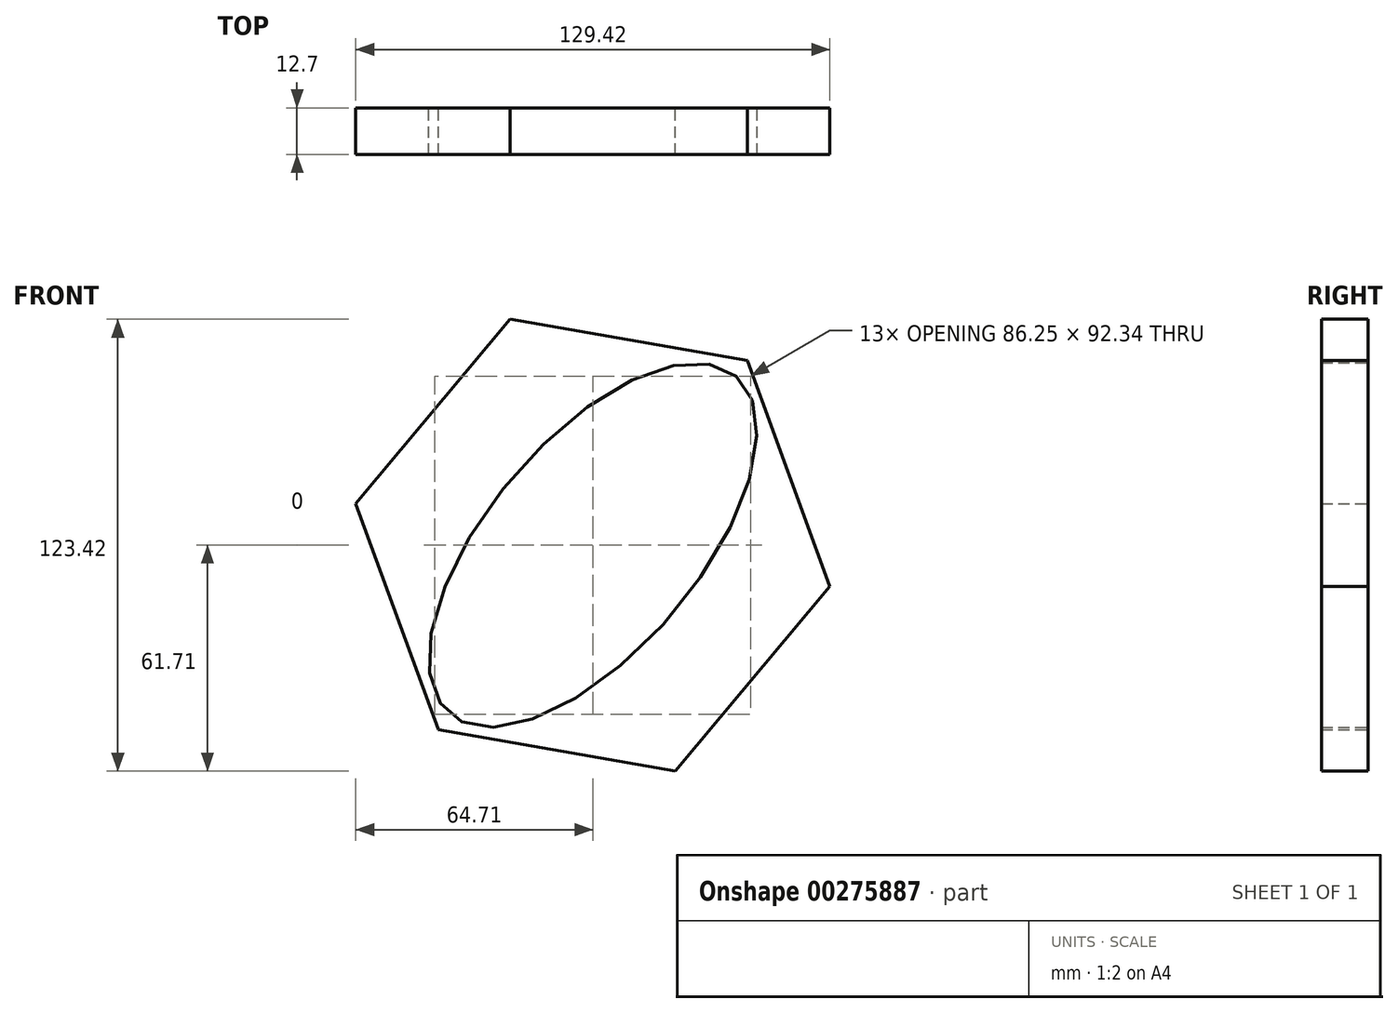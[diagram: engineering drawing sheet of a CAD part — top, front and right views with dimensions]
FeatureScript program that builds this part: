
annotation { "Feature Type Name" : "Feature", "Feature Type Description" : "" }
export const myFeature = defineFeature(function(context is Context, id is Id, definition is map)
    precondition{}
    {
        {
            var Q0;
            Q0=qCreatedBy(makeId("Front.planeOp"),FACE);
            var sketch = newSketch(context, id + "F0", { "sketchPlane" : qUnion([Q0])});
            skEllipse(sketch, "E0", {"center": v(0, 0) * mm, "majorRadius": 60.49 * mm, "minorRadius": 28.7 * mm, "majorAxis": v(0.65, 0.76)});
            skCircle(sketch, "E1.cCircle", {"center": v(0, 0) * mm, "radius": 56.9 * mm, "construction": true});
            skLineSegment(sketch, "E1.0", {"start": v(-22.54, 61.7) * mm, "end": v(42.17, 50.38) * mm});
            skLineSegment(sketch, "E1.1", {"start": v(42.17, 50.38) * mm, "end": v(64.71, -11.33) * mm});
            skLineSegment(sketch, "E1.2", {"start": v(64.71, -11.33) * mm, "end": v(22.54, -61.7) * mm});
            skLineSegment(sketch, "E1.3", {"start": v(22.54, -61.7) * mm, "end": v(-42.17, -50.38) * mm});
            skLineSegment(sketch, "E1.4", {"start": v(-42.17, -50.38) * mm, "end": v(-64.71, 11.33) * mm});
            skLineSegment(sketch, "E1.5", {"start": v(-64.71, 11.33) * mm, "end": v(-22.54, 61.7) * mm});
            skPoint(sketch, "E1.0.midPoint", {"position": v(9.81, 56.04) * mm});
            skSolve(sketch);
        }
        {
            var Q0;
            Q0 = qSketchRegion(id + "F0", true);
            extrude(context, id + "F1", {"entities" : qUnion([Q0]), "endBound" : BoundingType.SYMMETRIC, "depth" : 12.7 * mm});
        }
    });
